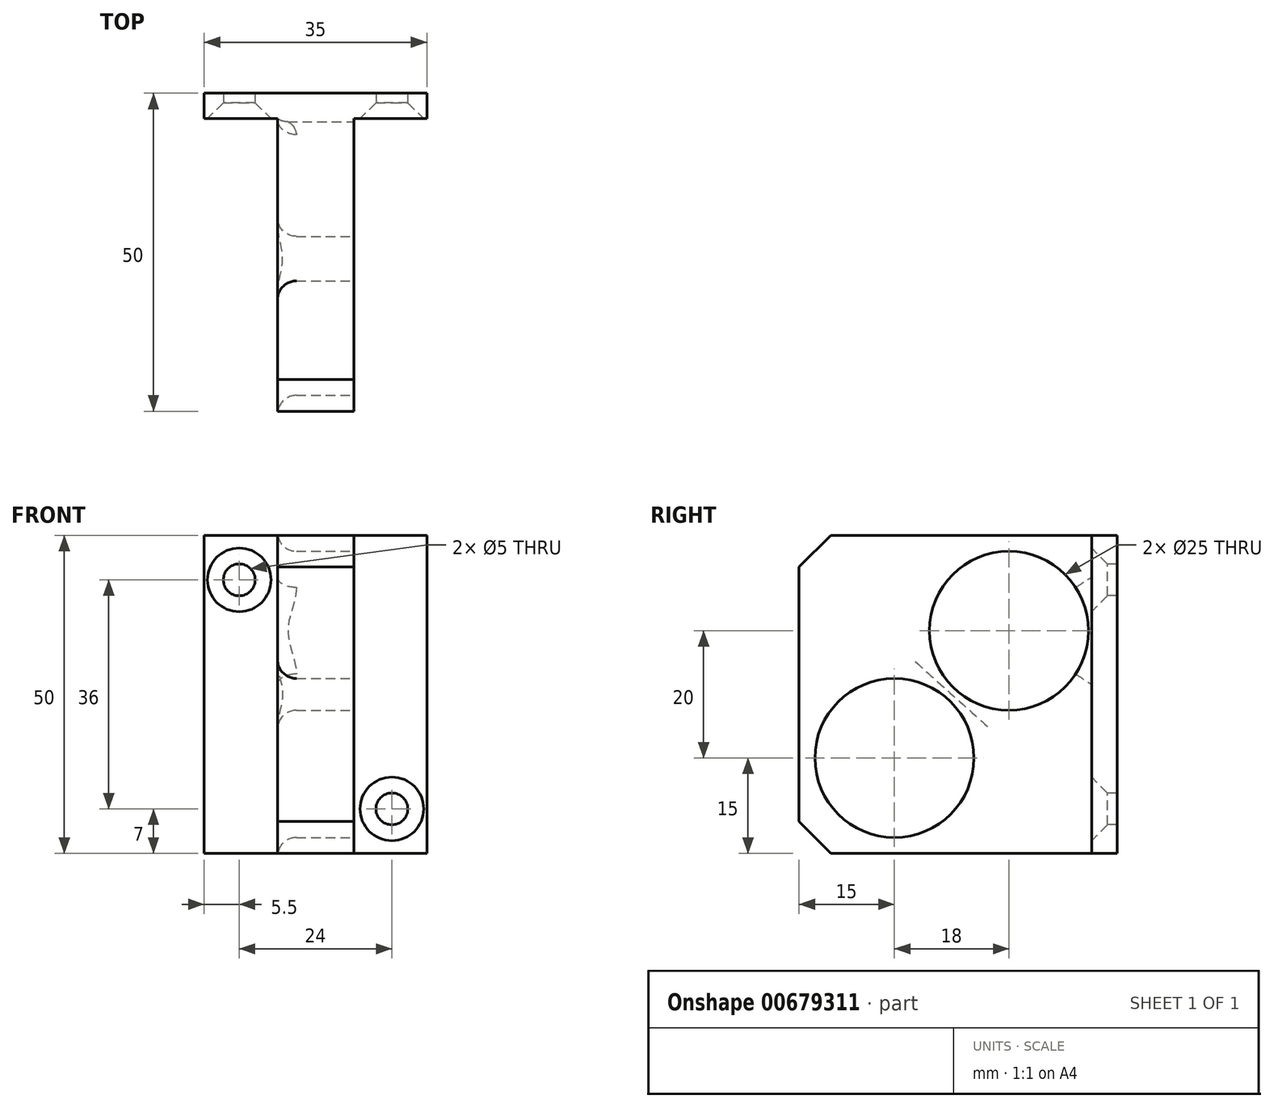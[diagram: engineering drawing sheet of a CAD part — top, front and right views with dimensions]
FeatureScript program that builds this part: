
annotation { "Feature Type Name" : "Feature", "Feature Type Description" : "" }
export const myFeature = defineFeature(function(context is Context, id is Id, definition is map)
    precondition{}
    {
        {
            var Q0;
            Q0=qCreatedBy(makeId("Front.planeOp"),FACE);
            var sketch = newSketch(context, id + "F0", { "sketchPlane" : qUnion([Q0])});
            skLineSegment(sketch, "E0.bottom", {"start": v(-6, 25) * mm, "end": v(6, 25) * mm});
            skLineSegment(sketch, "E0.top", {"start": v(-6, -25) * mm, "end": v(6, -25) * mm});
            skLineSegment(sketch, "E0.left", {"start": v(-6, 25) * mm, "end": v(-6, -25) * mm});
            skLineSegment(sketch, "E0.right", {"start": v(6, 25) * mm, "end": v(6, -25) * mm});
            skSolve(sketch);
        }
        {
            var Q0;
            Q0 = qSketchRegion(id + "F0", true);
            extrude(context, id + "F1", {"entities" : qUnion([Q0]), "depth" : 50 * mm, "offsetDistance" : 25 * mm});
        }
        {
            var Q0;
            Q0=makeQuery(id+"F1.opExtrude","SWEPT_FACE",FACE,{"disambiguationData":[OSD([sQuery(id+"F0.wireOp",EDGE,"E0.right")])]});
            var sketch = newSketch(context, id + "F2", { "sketchPlane" : qUnion([Q0])});
            skCircle(sketch, "E1", {"center": v(-17, 10) * mm, "radius": 12.5 * mm});
            skCircle(sketch, "E2", {"center": v(-35, -10) * mm, "radius": 12.5 * mm});
            skSolve(sketch);
        }
        {
            var Q0;
            Q0 = qSketchRegion(id + "F2", true);
            extrude(context, id + "F3", {"entities" : qUnion([Q0]), "operationType" : NewBodyOperationType.REMOVE, "endBound" : BoundingType.THROUGH_ALL, "oppositeDirection" : true, "depth" : 25 * mm, "offsetDistance" : 25 * mm});
        }
        {
            var Q0;
            Q0=qCreatedBy(makeId("Front.planeOp"),FACE);
            var sketch = newSketch(context, id + "F4", { "sketchPlane" : qUnion([Q0])});
            skLineSegment(sketch, "E3.bottom", {"start": v(-17.5, 25) * mm, "end": v(17.5, 25) * mm});
            skLineSegment(sketch, "E3.top", {"start": v(-17.5, -25) * mm, "end": v(17.5, -25) * mm});
            skLineSegment(sketch, "E3.left", {"start": v(-17.5, 25) * mm, "end": v(-17.5, -25) * mm});
            skLineSegment(sketch, "E3.right", {"start": v(17.5, 25) * mm, "end": v(17.5, -25) * mm});
            skPoint(sketch, "E4", {"position": v(0, 25) * mm});
            skSolve(sketch);
        }
        {
            var Q0;
            Q0 = qSketchRegion(id + "F4", true);
            extrude(context, id + "F5", {"entities" : qUnion([Q0]), "operationType" : NewBodyOperationType.ADD, "depth" : 4 * mm, "offsetDistance" : 25 * mm});
        }
        {
            var Q0;
            Q0=makeQuery(id+"F5.opExtrude","CAP_FACE",FACE,{"disambiguationData":[OSD([sQuery(id+"F4.wireOp",EDGE,"E3.bottom"),sQuery(id+"F4.wireOp",EDGE,"E3.top"),sQuery(id+"F4.wireOp",EDGE,"E3.left"),sQuery(id+"F4.wireOp",EDGE,"E3.right")])],"isStart":false});
            var sketch = newSketch(context, id + "F6", { "sketchPlane" : qUnion([Q0])});
            skPoint(sketch, "E5", {"position": v(-12, 18) * mm});
            skPoint(sketch, "E6", {"position": v(12, -18) * mm});
            skSolve(sketch);
        }
        {
            var Q0;
            Q0=sQuery(id+"F6.wireOp",VERTEX,"E5");
            var Q1;
            Q1=sQuery(id+"F6.wireOp",VERTEX,"E6");
            var Q2;
            Q2=makeQuery(id+"F1.opExtrude","SWEPT_BODY",BODY,{"disambiguationData":[OSD([sQuery(id+"F0.wireOp",EDGE,"E0.bottom"),sQuery(id+"F0.wireOp",EDGE,"E0.top"),sQuery(id+"F0.wireOp",EDGE,"E0.left"),sQuery(id+"F0.wireOp",EDGE,"E0.right")])]});
            hole(context, id + "F7", {"style" : HoleStyle.C_SINK, "endStyle" : HoleEndStyle.THROUGH, "holeDiameter" : 5 * mm, "cSinkDiameter" : 10 * mm, "cSinkAngle" : 90 * degree, "majorDiameter" : 5 * mm, "isTappedThrough" : true, "tappedDepth" : 12 * mm, "tapClearance" : 3, "startFromSketch" : true, "locations" : qUnion([Q0, Q1]), "scope" : qUnion([Q2])});
        }
        {
            var Q0;
            Q0=makeQuery(id+"F3.boolean.opBoolean","INTERSECT",EDGE,{"derivedFrom":[makeQuery(id+"F1.opExtrude","SWEPT_FACE",FACE,{"disambiguationData":[OSD([sQuery(id+"F0.wireOp",EDGE,"E0.left")])]}),makeQuery(id+"F3.opExtrude","SWEPT_FACE",FACE,{"disambiguationData":[OSD([sQuery(id+"F2.wireOp",EDGE,"E1")])]})]});
            var Q1;
            Q1=makeQuery(id+"F3.boolean.opBoolean","INTERSECT",EDGE,{"derivedFrom":[makeQuery(id+"F1.opExtrude","SWEPT_FACE",FACE,{"disambiguationData":[OSD([sQuery(id+"F0.wireOp",EDGE,"E0.left")])]}),makeQuery(id+"F3.opExtrude","SWEPT_FACE",FACE,{"disambiguationData":[OSD([sQuery(id+"F2.wireOp",EDGE,"E2")])]})]});
            var Q2;
            Q2=makeQuery(id+"F3.boolean.opBoolean","COPY",EDGE,{"derivedFrom":makeQuery(id+"F3.opExtrude","CAP_EDGE",EDGE,{"disambiguationData":[OSD([sQuery(id+"F2.wireOp",EDGE,"E1")])],"isStart":true})});
            var Q3;
            Q3=makeQuery(id+"F3.boolean.opBoolean","COPY",EDGE,{"derivedFrom":makeQuery(id+"F3.opExtrude","CAP_EDGE",EDGE,{"disambiguationData":[OSD([sQuery(id+"F2.wireOp",EDGE,"E2")])],"isStart":true})});
            fillet(context, id + "F8", {"entities" : qUnion([Q0, Q1, Q2, Q3]), "radius" : 3 * mm, "tangentPropagation" : true, "allowEdgeOverflow" : false});
        }
        {
            var Q0;
            Q0=makeQuery(id+"F1.opExtrude","CAP_EDGE",EDGE,{"disambiguationData":[OSD([sQuery(id+"F0.wireOp",EDGE,"E0.bottom")])],"isStart":false});
            var Q1;
            Q1=makeQuery(id+"F1.opExtrude","CAP_EDGE",EDGE,{"disambiguationData":[OSD([sQuery(id+"F0.wireOp",EDGE,"E0.top")])],"isStart":false});
            chamfer(context, id + "F9", {"entities" : qUnion([Q0, Q1]), "width" : 5 * mm, "tangentPropagation" : true});
        }
    });
